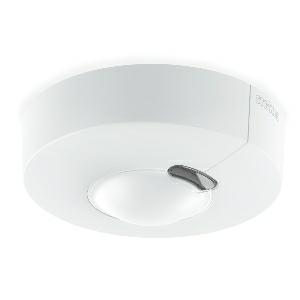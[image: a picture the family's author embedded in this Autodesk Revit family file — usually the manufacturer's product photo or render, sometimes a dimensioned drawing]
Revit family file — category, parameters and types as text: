
# Revit family: hf_3360_057329
name_source: partatom
category: Elektroinstallationen
revit_build: Autodesk Revit 2016 (Build: 20190508_0715(x64)
units: mm (PartAtom-declared; Revit-internal decimal feet)

## family parameters
Basisbauteil = Fläche
Beim Laden mit Abzugskörper schneiden = Nein
Bemaßung runder Anschluss = Durchmesser verwenden
Beschriftungsausrichtung beibehalten = Nein
Gemeinsam genutzt = Nein
Raumberechnungspunkt = Nein
Teiletyp = Normal

## types (1)
- HF 3360
    Apparent Load = 0 VA
    Beschreibung = Type: Motion detectors; Dimensions (Ø x H): 126 x 52 mm; Mains power supply: 12 – 22,5 V; Power consumption: 0,5 W; Sensor Technology: High frequency; Application, place: Indoors; Application, room: function room / ancillary room, stairwell, WC / washroom, multi-storey / underground car park, Indoors; Installation site: wall, ceiling, corner; Installation: Surface wiring; HF-system: 5,8 GHz; Electronic scalability: Yes; Mechanical scalability: No; Mounting height: 2,00 – 4,00 m; Optimum mounting height: 2,8 m; Detection: also through glass, wood and stud walls; Detection angle: 360 °; Angle of aperture: 160 °; Sneak-by guard: Yes; Reach, radial: Ø 8 m (50 m²); Reach, tangential: Ø 8 m (50 m²); Twilight setting TEACH: No; Twilight setting: 2 – 1000 lx; Control output, Dali: Addressable/slave; Constant-lighting control: No; Basic light level function: No; With bus coupling: Yes; Settings via: Bus; With remote control: No; IP-rating: IP54; Material: Plastic; Ambient temperature: -20 – 50 °C; Colour: white; Colour, RAL: 9003; Manufacturer's Warranty: 5 years; Version: DALI-2 IPD - surface, rd.; PU1, EAN: 4007841057329
    Height = 0 mm  [stored 0 ft]
    Hersteller = Steinel
    Length = 126 mm
    ModVariant = Nein
    Modell = 057329
    Mounting Type = Surface mounted
    Number of Poles = 1
    OnlyDefault = Ja
    Power Factor = 1
    Product Name = HF 3360
    Product group = Sensor-switched indoor light
    ProductGroupID = 30
    Protection Class = Protection class
    Protection Degree = IP 54
    RlxData = <blob elided: 37085 chars, md5=bab4f0e4>
    SensorDataFile = {"IESDataFiles":[]}
    Typenbild = produkt1_057329.jpg
    Typenkommentare = Product without accessories
    URL = http://relux.com
    VarID = ---
    Voltage = 0 V
    Vorgabe-Ansicht = 1800 mm
    Weight = 0.00 kg
    Width = 0 mm  [stored 0 ft]

note: [stored X ft] marks values corroborated as IEEE doubles in the binary element streams (Revit-internal decimal feet)

## geometry (parser evidence)
native form markers: Sweep x12
no freeform markers — native parametric forms only
